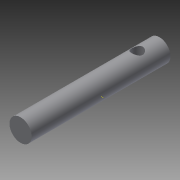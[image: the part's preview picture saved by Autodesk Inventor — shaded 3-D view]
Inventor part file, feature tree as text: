
AUTODESK INVENTOR PART (.ipt)
format: ipt  version: 2015 SP1 (Build 190203100, 203)  size: 84,992 bytes
history: native  units: mm
features: other x3, sketch x2, plane x1
ambient origin geometry x8: Origin, YZ Plane, XZ Plane, XY Plane, X Axis, Y Axis, Z Axis, Center Point
bodies: Solid1 (feature_tree)
feature tree (6):
  other  "Part3.ipt"
  other  "Solid2::Part3.ipt"
  other  "TaggingFeature1"
  sketch  "Sketch5"  dims[d0=10.0mm]
  sketch  "Sketch7"
  plane  "Work Plane1"
